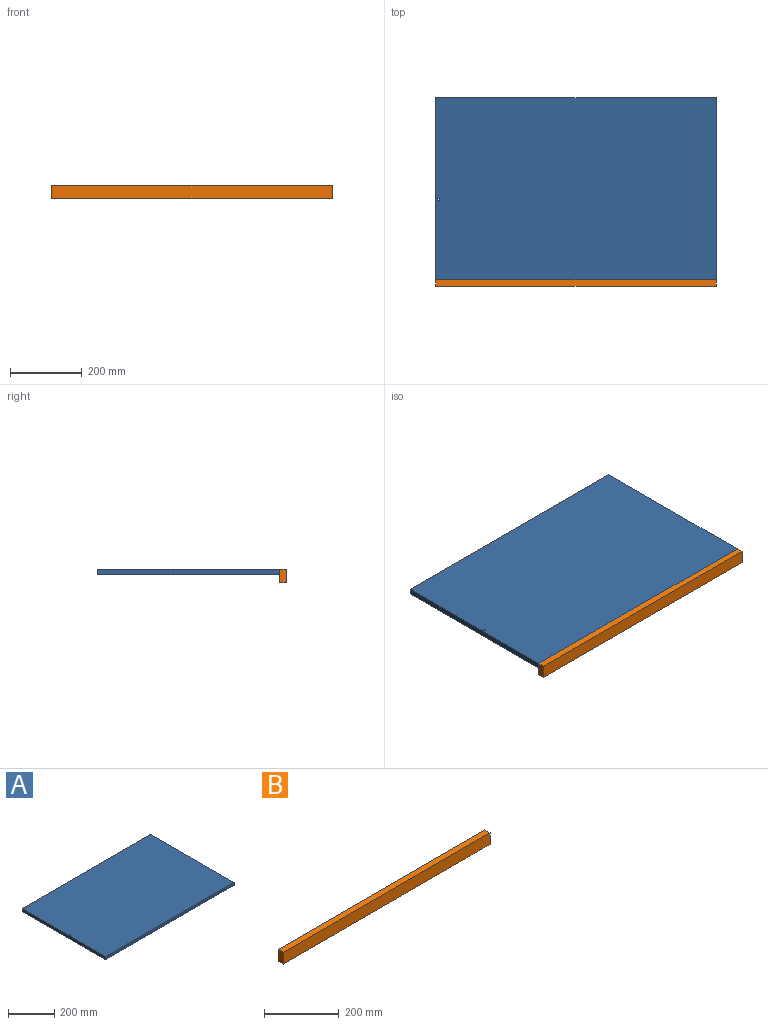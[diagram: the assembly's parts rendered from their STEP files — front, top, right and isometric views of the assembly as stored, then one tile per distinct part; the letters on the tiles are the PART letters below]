
ASSEMBLY  parts=2 mates=1
PART A: 7 faces, bbox 784.2x508x15.9 mm
  f0: plane 508x15.88mm, normal (-1,0,0), area 8064.5mm2, adj f1,f4,f5,f6
  f1: plane 784.23x15.88mm, normal (0,-1,0), area 12449.6mm2, adj f0,f2,f5,f6
  f2: plane 508x15.88mm, normal (1,0,0), area 8064.5mm2, adj f1,f4,f5,f6
  f3: cylinder r=3.17mm len=15.88mm, axis (0,0,-1), area 316.7mm2, adj f5,f6
  f4: plane 784.23x15.88mm, normal (0,1,0), area 12449.6mm2, adj f0,f2,f5,f6
  f5: plane 784.23x508mm, normal (0,0,1), area 398354.6mm2, adj f0,f1,f2,f3,f4
  f6: plane 784.23x508mm, normal (0,0,-1), area 398354.6mm2, adj f0,f1,f2,f3,f4
PART B: 6 faces, bbox 784.2x19.1x38.1 mm
  f0: plane 784.23x38.1mm, normal (0,1,0), area 29879mm2, adj f1,f3,f4,f5
  f1: plane 38.1x19.05mm, normal (-1,0,0), area 725.8mm2, adj f0,f2,f4,f5
  f2: plane 784.23x38.1mm, normal (0,-1,0), area 29879mm2, adj f1,f3,f4,f5
  f3: plane 38.1x19.05mm, normal (1,0,0), area 725.8mm2, adj f0,f2,f4,f5
  f4: plane 784.23x19.05mm, normal (0,0,1), area 14939.5mm2, adj f0,f1,f2,f3
  f5: plane 784.23x19.05mm, normal (0,0,-1), area 14939.5mm2, adj f0,f1,f2,f3
PLACE A t=(-207.42,376.02,-80.49)mm
PLACE B t=(-207.42,376.02,-102.71)mm
MATE fastened B.f0 <-> A.f1  axis (0,1,0) through (184.69,-131.98,52.86)mm
